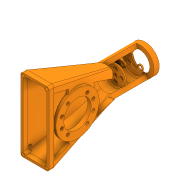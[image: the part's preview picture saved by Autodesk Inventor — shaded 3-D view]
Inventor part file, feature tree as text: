
AUTODESK INVENTOR PART (.ipt)
format: ipt  version: 2020 (Build 240168000, 168)  size: 1,408,512 bytes
history: native  units: in
note: dims shown in document units (in); Inventor stores cm internally (conversion verified against a paired STEP export)
features: sketch x27, extrude x24, projected_geometry x14, chamfer x4, plane x3, fillet x3, loft x2, other x1
ambient origin geometry x8: Origin, YZ Plane, XZ Plane, XY Plane, X Axis, Y Axis, Z Axis, Center Point
bodies: Solid1 (feature_tree)
feature tree (78):
  extrude  "Extrusion1"  Depth=2.0472in
  extrude  "Extrusion2"  Depth=0.2756in
  chamfer  "Chamfer1"  Distance=0.5512in
  extrude  "Extrusion3"  Depth=0.2756in
  extrude  "Extrusion4"  Depth=0.2756in TaperAngle=0.0deg
  extrude  "Extrusion5"  Depth=0.315in
  extrude  "Extrusion6"  Depth=0.4724in
  extrude  "Extrusion7"  Depth=0.0787in
  plane  "Work Plane1"
  extrude  "Extrusion8"  Depth=0.1575in
  plane  "Work Plane2"
  extrude  "Extrusion9"  Depth=1.0994in
  sketch  "Sketch11"  dims[d31=15.0deg d32=0.4921in d33=0.0in]
  plane  "Work Plane3"
  extrude  "Extrusion10"  Depth=0.4921in TaperAngle=0.0deg
  extrude  "Extrusion11"  Depth=1.5748in TaperAngle=360.0deg
  loft  "Loft1"
  loft  "Loft2"
  sketch  "Sketch16"  dims[d47=0.315in d48=0.4331in]
  extrude  "Extrusion12"  Depth=0.0984in TaperAngle=0.0deg
  extrude  "Extrusion13"  Depth=0.4331in
  extrude  "Extrusion14"  Depth=0.6161in
  extrude  "Extrusion15"  Depth=0.1575in
  fillet  "Fillet1"  Radius=0.0984in
  chamfer  "Chamfer23"  Distance=0.3484in
  extrude  "Extrusion19"  Depth=0.3937in
  extrude  "Extrusion20"  Depth=0.3937in
  extrude  "Extrusion21"  Depth=0.3937in
  extrude  "Extrusion22"  Depth=0.3937in
  extrude  "Extrusion23"  Depth=0.3937in TaperAngle=0.0deg
  extrude  "Extrusion24"  Depth=0.3937in TaperAngle=0.0deg
  extrude  "Extrusion25"  TaperAngle=0.0deg  [1 undecoded]
  chamfer  "Chamfer24"  Angle=90.0deg  [1 undecoded]
  extrude  "Extrusion26"  TaperAngle=0.0deg  [1 undecoded]
  fillet  "Fillet2"  [1 undecoded]
  fillet  "Fillet3"  Radius=0.7874in
  extrude  "Extrusion27"  Depth=0.3937in
  chamfer  "Chamfer25"  Distance=0.3937in
  sketch  "Sketch1"  dims[d0=2.3622in d1=2.0472in]
  sketch  "Sketch2"  dims[d2=0.2756in d3=0.0in d4=1.6535in d5=0.5512in d6=0.0in]
  sketch  "Sketch3"  dims[d7=0.2756in d8=0.125in d9=0.0137in d10=0.0157in]
  sketch  "Sketch5"  dims[d11=4.7244in d13=360.0deg d15=0.2756in d16=0.0in]
  sketch  "Sketch6"  dims[d17=0.5512in d19=0.315in]
  projected_geometry  "Projected Loop1"
  sketch  "Sketch7"  dims[d20=0.315in d21=0.4724in]
  projected_geometry  "Projected Loop2"
  sketch  "Sketch8"  dims[d22=0.4724in d23=0.0787in d24=0.0787in d25=0.0787in]
  projected_geometry  "Projected Loop3"
  sketch  "Sketch9"  dims[d26=0.0984in d27=0.0in d28=0.1575in]
  sketch  "Sketch10"  dims[d29=0.1575in d30=1.0994in]
  sketch  "Sketch12"  dims[d34=1.4567in d35=0.0in d36=1.5748in d38=360.0deg]
  sketch  "Sketch13"  dims[d40=0.0787in d41=0.0787in]
  projected_geometry  "Projected Loop4"
  other  "Edges1"
  sketch  "Sketch14"  dims[d42=0.0787in d43=0.0787in]
  projected_geometry  "Projected Loop5"
  sketch  "Sketch15"  dims[d44=0.0787in d45=0.0984in d46=0.0in]
  projected_geometry  "Projected Loop6"
  projected_geometry  "Projected Loop7"
  sketch  "Sketch19"  dims[d49=0.0984in d50=0.0in d51=0.6161in]
  projected_geometry  "Projected Loop8"
  sketch  "Sketch20"  dims[d52=0.1575in d53=0.1575in d54=0.0984in d55=0.0in]
  projected_geometry  "Projected Loop9"
  sketch  "Sketch21"  dims[d56=6.6929in]
  sketch  "Sketch25"  dims[d57=0.8858in]
  sketch  "Sketch26"  dims[d58=1.6654in]
  projected_geometry  "Projected Loop11"
  sketch  "Sketch27"  dims[d59=1.6654in]
  projected_geometry  "Projected Loop12"
  sketch  "Sketch28"  dims[d60=0.0in]
  sketch  "Sketch29"  dims[d61=0.0in]
  sketch  "Sketch30"  dims[d62=1.6654in]
  sketch  "Sketch31"  dims[d63=1.6654in]
  projected_geometry  "Projected Loop13"
  sketch  "Sketch32"  dims[d64=0.1969in]
  projected_geometry  "Projected Loop14"
  sketch  "Sketch33"  dims[d65=0.1969in d66=0.3484in d67=0.3484in d68=0.1969in d69=0.1969in d70=0.1969in d71=0.3937in d72=0.0in d73=0.7874in d74=0.0in d75=0.0in d76=90.0deg d77=0.0in d78=90.0deg d79=0.0in d80=90.0deg d81=0.0in d82=90.0deg d86=0.7874in d87=0.0in d90=0.3937in d91=0.3937in d92=0.7874in d93=0.0in d94=0.1969in d95=0.0in d96=0.8858in d97=1.6654in d98=1.6654in d99=0.0in d100=0.0in d101=0.2224in d102=0.1575in d103=0.1575in d104=0.1575in d105=0.1575in d106=0.0984in d107=0.0984in d108=0.1969in d109=0.0in d185=0.0315in d193=0.0984in d194=0.3937in d195=0.125in d196=45.0deg d197=0.2756in d198=0.1969in d199=0.0in d200=0.2756in d201=2.7559in d202=0.2756in d203=0.2756in d204=0.2756in d205=0.2756in d206=0.2756in d207=0.2756in d208=0.2756in d209=0.0394in d210=0.2047in d211=0.0in d212=0.1969in d213=0.2756in d214=0.0in d215=1.0in d216=0.0in d217=0.2362in d218=0.2362in d219=0.2362in d220=0.2362in d221=0.2362in d222=0.0in d223=0.3937in d224=0.0in d225=0.1575in d226=0.0in d227=0.315in d228=0.187in d229=0.125in d230=45.0deg d231=1.0in d232=0.0in d233=0.1969in d234=0.315in d235=0.4724in d236=0.0984in d237=0.0in d238=0.0984in d239=0.125in d240=45.0deg]
  projected_geometry  "Projected Loop15"
note: 4 required parameter values undecoded (feature->parameter linkage not recoverable at this tier; creation-order binding heuristic only, values carry confidence <= 0.55)
